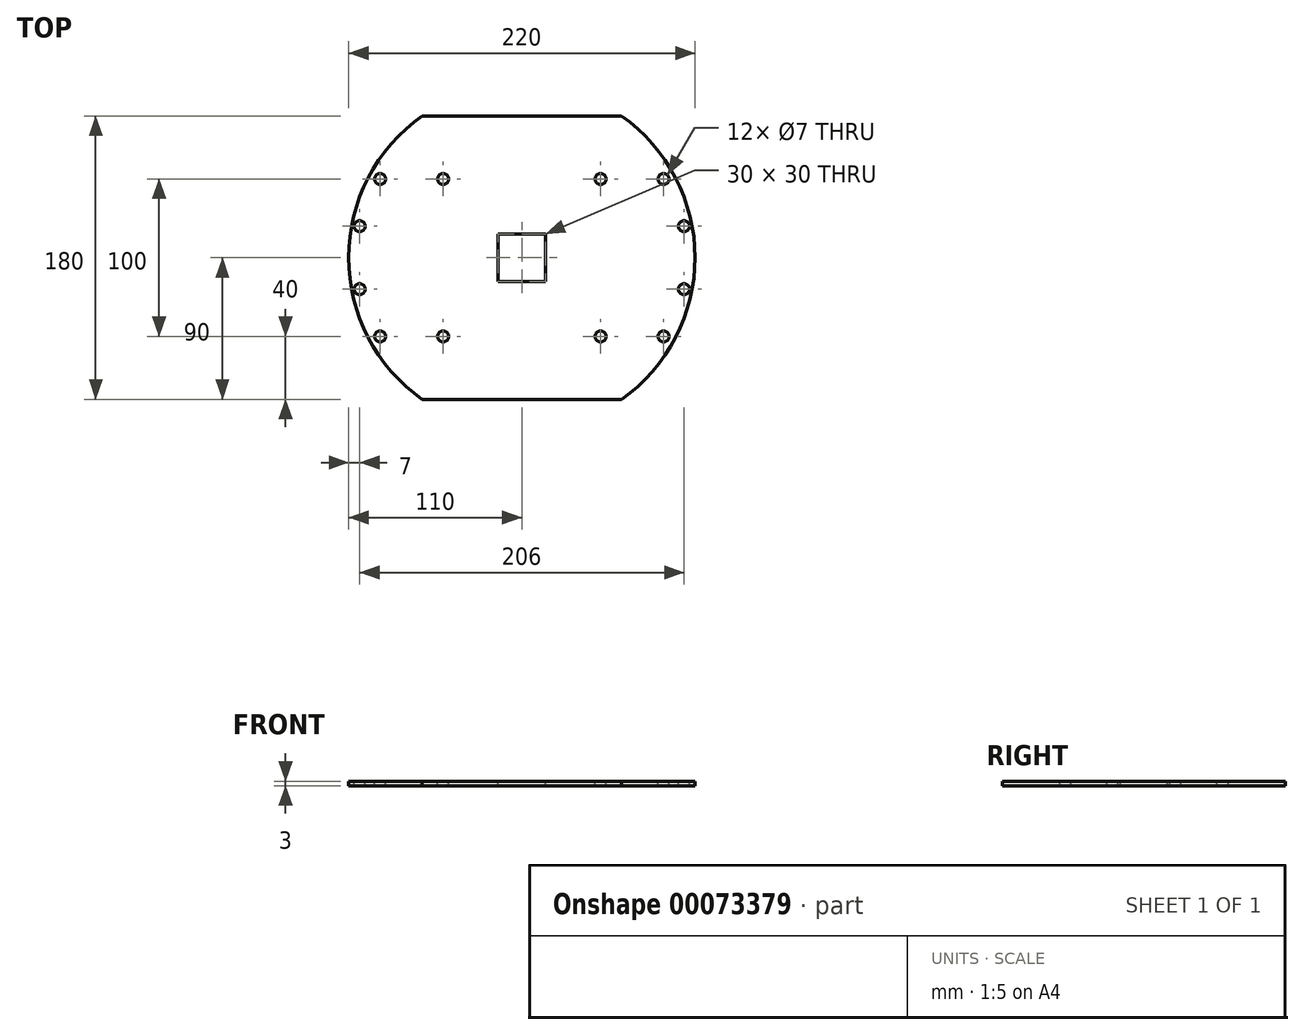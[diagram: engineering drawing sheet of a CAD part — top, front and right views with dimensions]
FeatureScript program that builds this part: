
annotation { "Feature Type Name" : "Feature", "Feature Type Description" : "" }
export const myFeature = defineFeature(function(context is Context, id is Id, definition is map)
    precondition{}
    {
        {
            var Q0;
            Q0=qCreatedBy(makeId("Top.planeOp"),FACE);
            var sketch = newSketch(context, id + "F0", { "sketchPlane" : qUnion([Q0])});
            skCircle(sketch, "E0", {"center": v(0, 0) * mm, "radius": 110 * mm, "construction": true});
            skLineSegment(sketch, "E1.bottom", {"start": v(-63.25, 90) * mm, "end": v(63.25, 90) * mm});
            skLineSegment(sketch, "E1.top", {"start": v(-63.25, -90) * mm, "end": v(63.25, -90) * mm});
            skLineSegment(sketch, "E1.left", {"start": v(-63.25, 90) * mm, "end": v(-63.25, -90) * mm, "construction": true});
            skLineSegment(sketch, "E1.right", {"start": v(63.25, 90) * mm, "end": v(63.25, -90) * mm, "construction": true});
            skArc(sketch, "E2", {"start": v(-63.25, -90) * mm, "mid": v(-110, 0) * mm, "end": v(-63.25, 90) * mm});
            skArc(sketch, "E3", {"start": v(63.25, 90) * mm, "mid": v(110, 0) * mm, "end": v(63.25, -90) * mm});
            skSolve(sketch);
        }
        {
            var Q0;
            Q0=makeQuery(id+"F0.imprint","IMPRINT",FACE,{"disambiguationData":[TD([[makeQuery(id+"F0.imprint","IMPRINT",EDGE,{"derivedFrom":sQuery(id+"F0.wireOp",EDGE,"E1.bottom")}),-1.0]])]});
            extrude(context, id + "F1", {"entities" : qUnion([Q0]), "depth" : 3 * mm, "offsetDistance" : 25 * mm});
        }
        {
            var Q0;
            Q0=makeQuery(id+"F1.opExtrude","CAP_FACE",FACE,{"disambiguationData":[OSD([sQuery(id+"F0.wireOp",EDGE,"E1.bottom"),sQuery(id+"F0.wireOp",EDGE,"E1.top"),sQuery(id+"F0.wireOp",EDGE,"E2"),sQuery(id+"F0.wireOp",EDGE,"E3")])],"isStart":false});
            var sketch = newSketch(context, id + "F2", { "sketchPlane" : qUnion([Q0])});
            skLineSegment(sketch, "E4.bottom", {"start": v(-98, 45) * mm, "end": v(-82, 45) * mm});
            skLineSegment(sketch, "E4.top", {"start": v(-98, -45) * mm, "end": v(-82, -45) * mm});
            skLineSegment(sketch, "E4.left", {"start": v(-98, 45) * mm, "end": v(-98, -45) * mm});
            skLineSegment(sketch, "E4.right", {"start": v(-82, 45) * mm, "end": v(-82, -45) * mm});
            skLineSegment(sketch, "E5.bottom", {"start": v(-95, 45) * mm, "end": v(-85, 45) * mm});
            skLineSegment(sketch, "E5.top", {"start": v(-95, 55) * mm, "end": v(-85, 55) * mm});
            skLineSegment(sketch, "E5.left", {"start": v(-95, 45) * mm, "end": v(-95, 55) * mm});
            skLineSegment(sketch, "E5.right", {"start": v(-85, 45) * mm, "end": v(-85, 55) * mm});
            skLineSegment(sketch, "E6.bottom", {"start": v(-95, -45) * mm, "end": v(-85, -45) * mm});
            skLineSegment(sketch, "E6.top", {"start": v(-95, -55) * mm, "end": v(-85, -55) * mm});
            skLineSegment(sketch, "E6.left", {"start": v(-95, -45) * mm, "end": v(-95, -55) * mm});
            skLineSegment(sketch, "E6.right", {"start": v(-85, -45) * mm, "end": v(-85, -55) * mm});
            skLineSegment(sketch, "E7.bottom", {"start": v(-109, 15) * mm, "end": v(-98, 15) * mm});
            skLineSegment(sketch, "E7.top", {"start": v(-109, -15) * mm, "end": v(-98, -15) * mm});
            skLineSegment(sketch, "E7.left", {"start": v(-109, 15) * mm, "end": v(-109, -15) * mm});
            skLineSegment(sketch, "E7.right", {"start": v(-98, 15) * mm, "end": v(-98, -15) * mm});
            skPoint(sketch, "E8", {"position": v(-98, 0) * mm});
            skPoint(sketch, "E9", {"position": v(-90, 45) * mm});
            skPoint(sketch, "E10", {"position": v(-90, -45) * mm});
            skLineSegment(sketch, "E11.bottom", {"start": v(-98, -15) * mm, "end": v(-108, -15) * mm});
            skLineSegment(sketch, "E11.top", {"start": v(-98, -25) * mm, "end": v(-108, -25) * mm});
            skLineSegment(sketch, "E11.left", {"start": v(-98, -15) * mm, "end": v(-98, -25) * mm});
            skLineSegment(sketch, "E11.right", {"start": v(-108, -15) * mm, "end": v(-108, -25) * mm});
            skLineSegment(sketch, "E12.bottom", {"start": v(-98, 15) * mm, "end": v(-108, 15) * mm});
            skLineSegment(sketch, "E12.top", {"start": v(-98, 25) * mm, "end": v(-108, 25) * mm});
            skLineSegment(sketch, "E12.left", {"start": v(-98, 15) * mm, "end": v(-98, 25) * mm});
            skLineSegment(sketch, "E12.right", {"start": v(-108, 15) * mm, "end": v(-108, 25) * mm});
            skLineSegment(sketch, "E13", {"start": v(-98, -15) * mm, "end": v(-108, -25) * mm});
            skLineSegment(sketch, "E14", {"start": v(-98, 15) * mm, "end": v(-108, 25) * mm});
            skPoint(sketch, "E15", {"position": v(-103, 20) * mm});
            skPoint(sketch, "E16", {"position": v(-103, -20) * mm});
            skLineSegment(sketch, "E17", {"start": v(-85, 45) * mm, "end": v(-95, 55) * mm});
            skLineSegment(sketch, "E18", {"start": v(-85, -45) * mm, "end": v(-95, -55) * mm});
            skPoint(sketch, "E19", {"position": v(-90, -50) * mm});
            skPoint(sketch, "E20", {"position": v(-90, 50) * mm});
            skLineSegment(sketch, "E21.MirrorCS", {"start": v(108, 15) * mm, "end": v(108, 25) * mm});
            skLineSegment(sketch, "E22.MirrorCS", {"start": v(98, 15) * mm, "end": v(98, 25) * mm});
            skLineSegment(sketch, "E23.MirrorCS", {"start": v(98, 15) * mm, "end": v(108, 15) * mm});
            skLineSegment(sketch, "E24.MirrorCS", {"start": v(108, -15) * mm, "end": v(108, -25) * mm});
            skLineSegment(sketch, "E25.MirrorCS", {"start": v(98, -15) * mm, "end": v(108, -15) * mm});
            skLineSegment(sketch, "E26.MirrorCS", {"start": v(98, 25) * mm, "end": v(108, 25) * mm});
            skLineSegment(sketch, "E27.MirrorCS", {"start": v(85, -45) * mm, "end": v(95, -55) * mm});
            skLineSegment(sketch, "E28.MirrorCS", {"start": v(95, -45) * mm, "end": v(85, -45) * mm});
            skLineSegment(sketch, "E29.MirrorCS", {"start": v(95, -55) * mm, "end": v(85, -55) * mm});
            skLineSegment(sketch, "E30.MirrorCS", {"start": v(95, -45) * mm, "end": v(95, -55) * mm});
            skLineSegment(sketch, "E31.MirrorCS", {"start": v(98, -15) * mm, "end": v(108, -25) * mm});
            skLineSegment(sketch, "E32.MirrorCS", {"start": v(98, 15) * mm, "end": v(108, 25) * mm});
            skLineSegment(sketch, "E33.MirrorCS", {"start": v(98, -15) * mm, "end": v(98, -25) * mm});
            skLineSegment(sketch, "E34.MirrorCS", {"start": v(85, -45) * mm, "end": v(85, -55) * mm});
            skLineSegment(sketch, "E35.MirrorCS", {"start": v(98, -25) * mm, "end": v(108, -25) * mm});
            skLineSegment(sketch, "E36.MirrorCS", {"start": v(98, 45) * mm, "end": v(82, 45) * mm});
            skLineSegment(sketch, "E37.MirrorCS", {"start": v(109, -15) * mm, "end": v(98, -15) * mm});
            skLineSegment(sketch, "E38.MirrorCS", {"start": v(98, -45) * mm, "end": v(82, -45) * mm});
            skLineSegment(sketch, "E39.MirrorCS", {"start": v(109, 15) * mm, "end": v(98, 15) * mm});
            skLineSegment(sketch, "E40.MirrorCS", {"start": v(95, 45) * mm, "end": v(95, 55) * mm});
            skLineSegment(sketch, "E41.MirrorCS", {"start": v(95, 45) * mm, "end": v(85, 45) * mm});
            skPoint(sketch, "E42.MirrorP", {"position": v(103, -20) * mm});
            skPoint(sketch, "E43.MirrorP", {"position": v(103, 20) * mm});
            skPoint(sketch, "E44.MirrorP", {"position": v(90, -50) * mm});
            skPoint(sketch, "E45.MirrorP", {"position": v(98, 0) * mm});
            skLineSegment(sketch, "E46.MirrorCS", {"start": v(85, 45) * mm, "end": v(95, 55) * mm});
            skLineSegment(sketch, "E47.MirrorCS", {"start": v(95, 55) * mm, "end": v(85, 55) * mm});
            skPoint(sketch, "E48.MirrorP", {"position": v(90, -45) * mm});
            skLineSegment(sketch, "E49.MirrorCS", {"start": v(98, 15) * mm, "end": v(98, -15) * mm});
            skPoint(sketch, "E50.MirrorP", {"position": v(90, 45) * mm});
            skPoint(sketch, "E51.MirrorP", {"position": v(90, 50) * mm});
            skLineSegment(sketch, "E52.MirrorCS", {"start": v(82, 45) * mm, "end": v(82, -45) * mm});
            skLineSegment(sketch, "E53.MirrorCS", {"start": v(109, 15) * mm, "end": v(109, -15) * mm});
            skLineSegment(sketch, "E54.MirrorCS", {"start": v(85, 45) * mm, "end": v(85, 55) * mm});
            skLineSegment(sketch, "E55.MirrorCS", {"start": v(98, 45) * mm, "end": v(98, -45) * mm});
            skSolve(sketch);
        }
        {
            var Q0;
            Q0=sQuery(id+"F2.wireOp",VERTEX,"f939c1bc-4f0a-46cc-9fde-5168f060ff73");
            var Q1;
            Q1=sQuery(id+"F2.wireOp",VERTEX,"E15");
            var Q2;
            Q2=sQuery(id+"F2.wireOp",VERTEX,"E16");
            var Q3;
            Q3=sQuery(id+"F2.wireOp",VERTEX,"12f0103e-799c-4177-9ba6-3f1d33425432");
            var Q4;
            Q4=sQuery(id+"F2.wireOp",VERTEX,"2fcbc748-485c-401b-9c6b-515daa93bae028.MirrorP");
            var Q5;
            Q5=sQuery(id+"F2.wireOp",VERTEX,"2fcbc748-485c-401b-9c6b-515daa93bae018.MirrorP");
            var Q6;
            Q6=sQuery(id+"F2.wireOp",VERTEX,"2fcbc748-485c-401b-9c6b-515daa93bae030.MirrorP");
            var Q7;
            Q7=sQuery(id+"F2.wireOp",VERTEX,"2fcbc748-485c-401b-9c6b-515daa93bae022.MirrorP");
            var Q8;
            Q8=sQuery(id+"F2.wireOp",VERTEX,"E20");
            var Q9;
            Q9=sQuery(id+"F2.wireOp",VERTEX,"E19");
            var Q10;
            Q10=sQuery(id+"F2.wireOp",VERTEX,"E44.MirrorP");
            var Q11;
            Q11=sQuery(id+"F2.wireOp",VERTEX,"E51.MirrorP");
            var Q12;
            Q12=sQuery(id+"F2.wireOp",VERTEX,"E43.MirrorP");
            var Q13;
            Q13=sQuery(id+"F2.wireOp",VERTEX,"E42.MirrorP");
            var Q14;
            Q14=makeQuery(id+"F1.opExtrude","SWEPT_BODY",BODY,{"disambiguationData":[OSD([sQuery(id+"F0.wireOp",EDGE,"E1.bottom"),sQuery(id+"F0.wireOp",EDGE,"E1.top"),sQuery(id+"F0.wireOp",EDGE,"E2"),sQuery(id+"F0.wireOp",EDGE,"E3")])]});
            hole(context, id + "F3", {"style" : HoleStyle.SIMPLE, "endStyle" : HoleEndStyle.THROUGH, "holeDiameter" : 7 * mm, "majorDiameter" : 5 * mm, "tappedDepth" : 12 * mm, "tapClearance" : 3, "locations" : qUnion([Q0, Q1, Q2, Q3, Q4, Q5, Q6, Q7, Q8, Q9, Q10, Q11, Q12, Q13]), "scope" : qUnion([Q14])});
        }
        {
            var Q0;
            Q0=makeQuery(id+"F1.opExtrude","CAP_FACE",FACE,{"disambiguationData":[OSD([sQuery(id+"F0.wireOp",EDGE,"E1.bottom"),sQuery(id+"F0.wireOp",EDGE,"E1.top"),sQuery(id+"F0.wireOp",EDGE,"E2"),sQuery(id+"F0.wireOp",EDGE,"E3")])],"isStart":false});
            var sketch = newSketch(context, id + "F4", { "sketchPlane" : qUnion([Q0])});
            skLineSegment(sketch, "E56.bottom", {"start": v(-50, 50) * mm, "end": v(50, 50) * mm});
            skLineSegment(sketch, "E56.top", {"start": v(-50, -50) * mm, "end": v(50, -50) * mm});
            skLineSegment(sketch, "E56.left", {"start": v(-50, 50) * mm, "end": v(-50, -50) * mm});
            skLineSegment(sketch, "E56.right", {"start": v(50, 50) * mm, "end": v(50, -50) * mm});
            skLineSegment(sketch, "E57", {"start": v(-50, 50) * mm, "end": v(50, -50) * mm, "construction": true});
            skPoint(sketch, "E58", {"position": v(0, 0) * mm});
            skSolve(sketch);
        }
        {
            var Q0;
            Q0=sQuery(id+"F4.wireOp",VERTEX,"E56.bottom.start");
            var Q1;
            Q1=sQuery(id+"F4.wireOp",VERTEX,"E56.bottom.end");
            var Q2;
            Q2=sQuery(id+"F4.wireOp",VERTEX,"E56.top.end");
            var Q3;
            Q3=sQuery(id+"F4.wireOp",VERTEX,"E56.top.start");
            var Q4;
            Q4=makeQuery(id+"F1.opExtrude","SWEPT_BODY",BODY,{"disambiguationData":[OSD([sQuery(id+"F0.wireOp",EDGE,"E1.bottom"),sQuery(id+"F0.wireOp",EDGE,"E1.top"),sQuery(id+"F0.wireOp",EDGE,"E2"),sQuery(id+"F0.wireOp",EDGE,"E3")])]});
            hole(context, id + "F5", {"style" : HoleStyle.SIMPLE, "endStyle" : HoleEndStyle.THROUGH, "holeDiameter" : 7 * mm, "majorDiameter" : 5 * mm, "tappedDepth" : 12 * mm, "tapClearance" : 3, "locations" : qUnion([Q0, Q1, Q2, Q3]), "scope" : qUnion([Q4])});
        }
        {
            var Q0;
            Q0=makeQuery(id+"F1.opExtrude","CAP_FACE",FACE,{"disambiguationData":[OSD([sQuery(id+"F0.wireOp",EDGE,"E1.bottom"),sQuery(id+"F0.wireOp",EDGE,"E1.top"),sQuery(id+"F0.wireOp",EDGE,"E2"),sQuery(id+"F0.wireOp",EDGE,"E3")])],"isStart":false});
            var sketch = newSketch(context, id + "F6", { "sketchPlane" : qUnion([Q0])});
            skLineSegment(sketch, "E59.bottom", {"start": v(-15, 15) * mm, "end": v(15, 15) * mm});
            skLineSegment(sketch, "E59.top", {"start": v(-15, -15) * mm, "end": v(15, -15) * mm});
            skLineSegment(sketch, "E59.left", {"start": v(-15, 15) * mm, "end": v(-15, -15) * mm});
            skLineSegment(sketch, "E59.right", {"start": v(15, 15) * mm, "end": v(15, -15) * mm});
            skLineSegment(sketch, "E60", {"start": v(-15, 15) * mm, "end": v(15, -15) * mm, "construction": true});
            skPoint(sketch, "E61", {"position": v(0, 0) * mm});
            skSolve(sketch);
        }
        {
            var Q0;
            Q0=makeQuery(id+"F6.imprint","IMPRINT",FACE,{"disambiguationData":[TD([[makeQuery(id+"F6.imprint","IMPRINT",EDGE,{"derivedFrom":sQuery(id+"F6.wireOp",EDGE,"E59.bottom")}),-1.0]])]});
            extrude(context, id + "F7", {"entities" : qUnion([Q0]), "operationType" : NewBodyOperationType.REMOVE, "endBound" : BoundingType.THROUGH_ALL, "oppositeDirection" : true, "depth" : 25 * mm, "offsetDistance" : 25 * mm});
        }
    });
